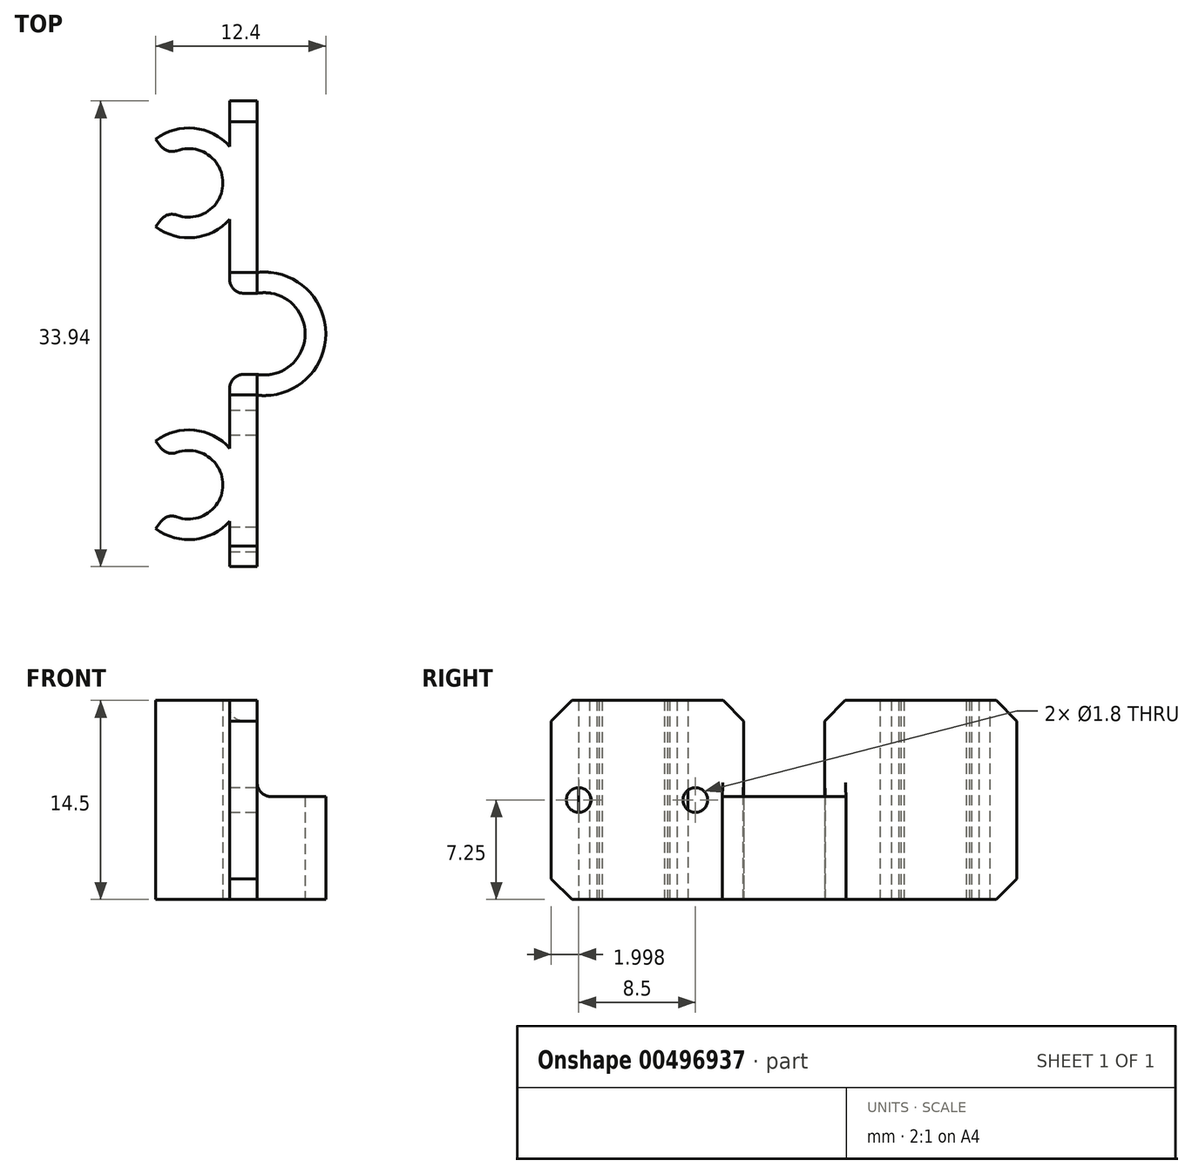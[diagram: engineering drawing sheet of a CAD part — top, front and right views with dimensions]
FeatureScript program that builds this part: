
annotation { "Feature Type Name" : "Feature", "Feature Type Description" : "" }
export const myFeature = defineFeature(function(context is Context, id is Id, definition is map)
    precondition{}
    {
        {
            var Q0;
            Q0=qCreatedBy(makeId("Top.planeOp"),FACE);
            var sketch = newSketch(context, id + "F0", { "sketchPlane" : qUnion([Q0])});
            skLineSegment(sketch, "E0.left", {"start": v(5, 15) * mm, "end": v(5, 4.47) * mm});
            skPoint(sketch, "E0.middle", {"position": v(0, 0) * mm});
            skArc(sketch, "E1", {"start": v(-1.5, 9) * mm, "mid": v(2.5, 11) * mm, "end": v(-1.5, 13) * mm});
            skArc(sketch, "E2", {"start": v(-2.4, 7.8) * mm, "mid": v(4, 11) * mm, "end": v(-2.4, 14.2) * mm});
            skArc(sketch, "E3", {"start": v(8.5, 0) * mm, "mid": v(7.44, 2.3) * mm, "end": v(5, 2.96) * mm});
            skArc(sketch, "E4", {"start": v(10, 0) * mm, "mid": v(8.5, 3.35) * mm, "end": v(5, 4.47) * mm});
            skLineSegment(sketch, "E5", {"start": v(-1.5, 13) * mm, "end": v(-2.4, 14.2) * mm});
            skLineSegment(sketch, "E6.MirrorCS", {"start": v(-1.5, 9) * mm, "end": v(-2.4, 7.8) * mm});
            skLineSegment(sketch, "E7", {"start": v(5, 2.96) * mm, "end": v(3, 2.96) * mm});
            skLineSegment(sketch, "E8", {"start": v(3, 2.96) * mm, "end": v(3, 8.35) * mm});
            skLineSegment(sketch, "E9", {"start": v(3, 15) * mm, "end": v(3, 16.97) * mm});
            skLineSegment(sketch, "E10", {"start": v(3, 16.97) * mm, "end": v(5, 16.97) * mm});
            skLineSegment(sketch, "E11", {"start": v(5, 16.97) * mm, "end": v(5, 15) * mm});
            skLineSegment(sketch, "E12", {"start": v(3, 15) * mm, "end": v(3, 13.65) * mm});
            skLineSegment(sketch, "E13.MirrorCS", {"start": v(-1.5, -13) * mm, "end": v(-2.4, -14.2) * mm});
            skLineSegment(sketch, "E14.MirrorCS", {"start": v(-1.5, -9) * mm, "end": v(-2.4, -7.8) * mm});
            skArc(sketch, "E15.MirrorCS", {"start": v(-1.5, -9) * mm, "mid": v(2.5, -11) * mm, "end": v(-1.5, -13) * mm});
            skArc(sketch, "E16.MirrorCS", {"start": v(-2.4, -7.8) * mm, "mid": v(4, -11) * mm, "end": v(-2.4, -14.2) * mm});
            skLineSegment(sketch, "E17.MirrorCS", {"start": v(3, -15) * mm, "end": v(3, -13.65) * mm});
            skLineSegment(sketch, "E18.MirrorCS", {"start": v(3, -15) * mm, "end": v(3, -16.97) * mm});
            skLineSegment(sketch, "E19.MirrorCS", {"start": v(3, -16.97) * mm, "end": v(5, -16.97) * mm});
            skLineSegment(sketch, "E20.MirrorCS", {"start": v(5, -16.97) * mm, "end": v(5, -15) * mm});
            skLineSegment(sketch, "E21.MirrorCS", {"start": v(5, -15) * mm, "end": v(5, -4.47) * mm});
            skArc(sketch, "E22.MirrorCS", {"start": v(8.5, 0) * mm, "mid": v(7.44, -2.3) * mm, "end": v(5, -2.96) * mm});
            skArc(sketch, "E23.MirrorCS", {"start": v(10, 0) * mm, "mid": v(8.5, -3.35) * mm, "end": v(5, -4.47) * mm});
            skLineSegment(sketch, "E24.MirrorCS", {"start": v(5, -2.96) * mm, "end": v(3, -2.96) * mm});
            skLineSegment(sketch, "E25.MirrorCS", {"start": v(3, -2.96) * mm, "end": v(3, -8.35) * mm});
            skSolve(sketch);
        }
        {
            var Q0;
            Q0=makeQuery(id+"F0.imprint","IMPRINT",FACE,{"disambiguationData":[TD([[makeQuery(id+"F0.imprint","IMPRINT",EDGE,{"derivedFrom":sQuery(id+"F0.wireOp",EDGE,"E0.left")}),-1.0]])]});
            extrude(context, id + "F1", {"entities" : qUnion([Q0]), "depth" : 14.5 * mm});
        }
        {
            var Q0;
            Q0=makeQuery(id+"F0.imprint","IMPRINT",FACE,{"disambiguationData":[TD([[makeQuery(id+"F0.imprint","IMPRINT",EDGE,{"derivedFrom":sQuery(id+"F0.wireOp",EDGE,"E1")}),-1.0]])]});
            var Q1;
            {var subQ3=sQuery(id+"F0.wireOp",EDGE,"E13.MirrorCS");Q1=makeQuery(id+"F0.imprint","IMPRINT",FACE,{"disambiguationData":[TD([[makeQuery(id+"F0.imprint","IMPRINT",EDGE,{"derivedFrom":subQ3}),1.0]])]});}
            extrude(context, id + "F2", {"entities" : qUnion([Q0, Q1]), "operationType" : NewBodyOperationType.ADD, "depth" : 14.5 * mm});
        }
        {
            var Q0;
            {var subQ0=sQuery(id+"F0.wireOp",EDGE,"E16.MirrorCS");var subQ1=sQuery(id+"F0.wireOp",EDGE,"E2");Q0=makeQuery(id+"F2.boolean.opBoolean","MERGE",FACE,{"derivedFrom":[makeQuery(id+"F1.opExtrude","CAP_FACE",FACE,{"disambiguationData":[OSD([sQuery(id+"F0.wireOp",EDGE,"E0.left"),subQ1,sQuery(id+"F0.wireOp",EDGE,"E3"),sQuery(id+"F0.wireOp",EDGE,"E4"),sQuery(id+"F0.wireOp",EDGE,"E7"),sQuery(id+"F0.wireOp",EDGE,"E8"),sQuery(id+"F0.wireOp",EDGE,"E9"),sQuery(id+"F0.wireOp",EDGE,"E10"),sQuery(id+"F0.wireOp",EDGE,"E11"),sQuery(id+"F0.wireOp",EDGE,"E12"),subQ0,sQuery(id+"F0.wireOp",EDGE,"E17.MirrorCS"),sQuery(id+"F0.wireOp",EDGE,"E18.MirrorCS"),sQuery(id+"F0.wireOp",EDGE,"E19.MirrorCS"),sQuery(id+"F0.wireOp",EDGE,"E20.MirrorCS"),sQuery(id+"F0.wireOp",EDGE,"E21.MirrorCS"),sQuery(id+"F0.wireOp",EDGE,"E22.MirrorCS"),sQuery(id+"F0.wireOp",EDGE,"E23.MirrorCS"),sQuery(id+"F0.wireOp",EDGE,"E24.MirrorCS"),sQuery(id+"F0.wireOp",EDGE,"E25.MirrorCS")])],"isStart":false}),makeQuery(id+"F2.opExtrude","CAP_FACE",FACE,{"disambiguationData":[OSD([sQuery(id+"F0.wireOp",EDGE,"E1"),subQ1,sQuery(id+"F0.wireOp",EDGE,"E5"),sQuery(id+"F0.wireOp",EDGE,"E6.MirrorCS")])],"isStart":false}),makeQuery(id+"F2.opExtrude","CAP_FACE",FACE,{"disambiguationData":[OSD([sQuery(id+"F0.wireOp",EDGE,"E13.MirrorCS"),sQuery(id+"F0.wireOp",EDGE,"E14.MirrorCS"),sQuery(id+"F0.wireOp",EDGE,"E15.MirrorCS"),subQ0])],"isStart":false})]});}
            var sketch = newSketch(context, id + "F3", { "sketchPlane" : qUnion([Q0])});
            skLineSegment(sketch, "E26", {"start": v(5, -4.47) * mm, "end": v(5, -2.96) * mm});
            skLineSegment(sketch, "E27", {"start": v(5, 4.47) * mm, "end": v(5, 2.96) * mm});
            skSolve(sketch);
        }
        {
            var Q0;
            Q0=makeQuery(id+"F3.imprint","IMPRINT",FACE,{"disambiguationData":[TD([[makeQuery(id+"F3.imprint","IMPRINT",EDGE,{"derivedFrom":sQuery(id+"F3.wireOp",EDGE,"E26")}),-1.0]])]});
            extrude(context, id + "F4", {"entities" : qUnion([Q0]), "operationType" : NewBodyOperationType.REMOVE, "oppositeDirection" : true, "depth" : 7 * mm});
        }
        {
            var Q0;
            Q0=makeQuery(id+"F4.boolean.opBoolean","MERGE",FACE,{"derivedFrom":[makeQuery(id+"F1.opExtrude","SWEPT_FACE",FACE,{"disambiguationData":[OSD([sQuery(id+"F0.wireOp",EDGE,"E20.MirrorCS"),sQuery(id+"F0.wireOp",EDGE,"E21.MirrorCS")])]}),makeQuery(id+"F4.opExtrude","SWEPT_FACE",FACE,{"disambiguationData":[OSD([sQuery(id+"F3.wireOp",EDGE,"E26")])]})]});
            var sketch = newSketch(context, id + "F5", { "sketchPlane" : qUnion([Q0])});
            skCircle(sketch, "E28", {"center": v(-14.97, 7.25) * mm, "radius": 0.9 * mm});
            skCircle(sketch, "E29", {"center": v(-6.47, 7.25) * mm, "radius": 0.9 * mm});
            skCircle(sketch, "E30.MirrorC", {"center": v(6.47, 7.25) * mm, "radius": 0.9 * mm});
            skCircle(sketch, "E31.MirrorC", {"center": v(14.97, 7.25) * mm, "radius": 0.9 * mm});
            skSolve(sketch);
        }
        {
            var Q0;
            Q0=makeQuery(id+"F5.imprint","IMPRINT",FACE,{"disambiguationData":[TD([[makeQuery(id+"F5.imprint","IMPRINT",EDGE,{"derivedFrom":sQuery(id+"F5.wireOp",EDGE,"E28")}),1.0]])]});
            var Q1;
            Q1=makeQuery(id+"F5.imprint","IMPRINT",FACE,{"disambiguationData":[TD([[makeQuery(id+"F5.imprint","IMPRINT",EDGE,{"derivedFrom":sQuery(id+"F5.wireOp",EDGE,"E29")}),1.0]])]});
            var Q2;
            Q2=makeQuery(id+"F5.imprint","IMPRINT",FACE,{"disambiguationData":[TD([[makeQuery(id+"F5.imprint","IMPRINT",EDGE,{"derivedFrom":sQuery(id+"F5.wireOp",EDGE,"E30.MirrorC")}),-1.0]])]});
            var Q3;
            Q3=makeQuery(id+"F5.imprint","IMPRINT",FACE,{"disambiguationData":[TD([[makeQuery(id+"F5.imprint","IMPRINT",EDGE,{"derivedFrom":sQuery(id+"F5.wireOp",EDGE,"E31.MirrorC")}),-1.0]])]});
            extrude(context, id + "F6", {"entities" : qUnion([Q0, Q1, Q2, Q3]), "operationType" : NewBodyOperationType.REMOVE, "oppositeDirection" : true, "depth" : 2 * mm});
        }
        {
            var Q0;
            Q0=makeQuery(id+"F1.opExtrude","CAP_EDGE",EDGE,{"disambiguationData":[OSD([sQuery(id+"F0.wireOp",EDGE,"E19.MirrorCS")])],"isStart":false});
            var Q1;
            Q1=makeQuery(id+"F1.opExtrude","CAP_EDGE",EDGE,{"disambiguationData":[OSD([sQuery(id+"F0.wireOp",EDGE,"E19.MirrorCS")])],"isStart":true});
            var Q2;
            Q2=makeQuery(id+"F1.opExtrude","CAP_EDGE",EDGE,{"disambiguationData":[OSD([sQuery(id+"F0.wireOp",EDGE,"E10")])],"isStart":true});
            var Q3;
            Q3=makeQuery(id+"F1.opExtrude","CAP_EDGE",EDGE,{"disambiguationData":[OSD([sQuery(id+"F0.wireOp",EDGE,"E10")])],"isStart":false});
            var Q4;
            Q4=makeQuery(id+"F1.opExtrude","CAP_EDGE",EDGE,{"disambiguationData":[OSD([sQuery(id+"F0.wireOp",EDGE,"E7")])],"isStart":false});
            var Q5;
            Q5=makeQuery(id+"F1.opExtrude","CAP_EDGE",EDGE,{"disambiguationData":[OSD([sQuery(id+"F0.wireOp",EDGE,"E24.MirrorCS")])],"isStart":false});
            chamfer(context, id + "F7", {"entities" : qUnion([Q0, Q1, Q2, Q3, Q4, Q5]), "width" : 1.5 * mm, "tangentPropagation" : true});
        }
        {
            var Q0;
            Q0=makeQuery(id+"F2.opExtrude","SWEPT_EDGE",EDGE,{"disambiguationData":[OSD([sQuery(id+"F0.wireOp",EDGE,"E14.MirrorCS"),sQuery(id+"F0.wireOp",EDGE,"E15.MirrorCS")])]});
            var Q1;
            Q1=makeQuery(id+"F2.opExtrude","SWEPT_EDGE",EDGE,{"disambiguationData":[OSD([sQuery(id+"F0.wireOp",EDGE,"E1"),sQuery(id+"F0.wireOp",EDGE,"E5")])]});
            var Q2;
            Q2=makeQuery(id+"F2.opExtrude","SWEPT_EDGE",EDGE,{"disambiguationData":[OSD([sQuery(id+"F0.wireOp",EDGE,"E13.MirrorCS"),sQuery(id+"F0.wireOp",EDGE,"E15.MirrorCS")])]});
            var Q3;
            Q3=makeQuery(id+"F2.opExtrude","SWEPT_EDGE",EDGE,{"disambiguationData":[OSD([sQuery(id+"F0.wireOp",EDGE,"E1"),sQuery(id+"F0.wireOp",EDGE,"E6.MirrorCS")])]});
            var Q4;
            Q4=makeQuery(id+"F4.boolean.opBoolean","COPY",EDGE,{"derivedFrom":makeQuery(id+"F4.opExtrude","CAP_EDGE",EDGE,{"disambiguationData":[OSD([sQuery(id+"F3.wireOp",EDGE,"E26")])],"isStart":false})});
            var Q5;
            Q5=makeQuery(id+"F4.boolean.opBoolean","COPY",EDGE,{"derivedFrom":makeQuery(id+"F4.opExtrude","CAP_EDGE",EDGE,{"disambiguationData":[OSD([sQuery(id+"F3.wireOp",EDGE,"E27")])],"isStart":false})});
            var Q6;
            Q6=makeQuery(id+"F1.opExtrude","SWEPT_EDGE",EDGE,{"disambiguationData":[OSD([sQuery(id+"F0.wireOp",EDGE,"E7"),sQuery(id+"F0.wireOp",EDGE,"E8")])]});
            var Q7;
            Q7=makeQuery(id+"F1.opExtrude","SWEPT_EDGE",EDGE,{"disambiguationData":[OSD([sQuery(id+"F0.wireOp",EDGE,"E24.MirrorCS"),sQuery(id+"F0.wireOp",EDGE,"E25.MirrorCS")])]});
            fillet(context, id + "F8", {"entities" : qUnion([Q0, Q1, Q2, Q3, Q4, Q5, Q6, Q7]), "radius" : 1 * mm, "tangentPropagation" : true, "allowEdgeOverflow" : false});
        }
    });
